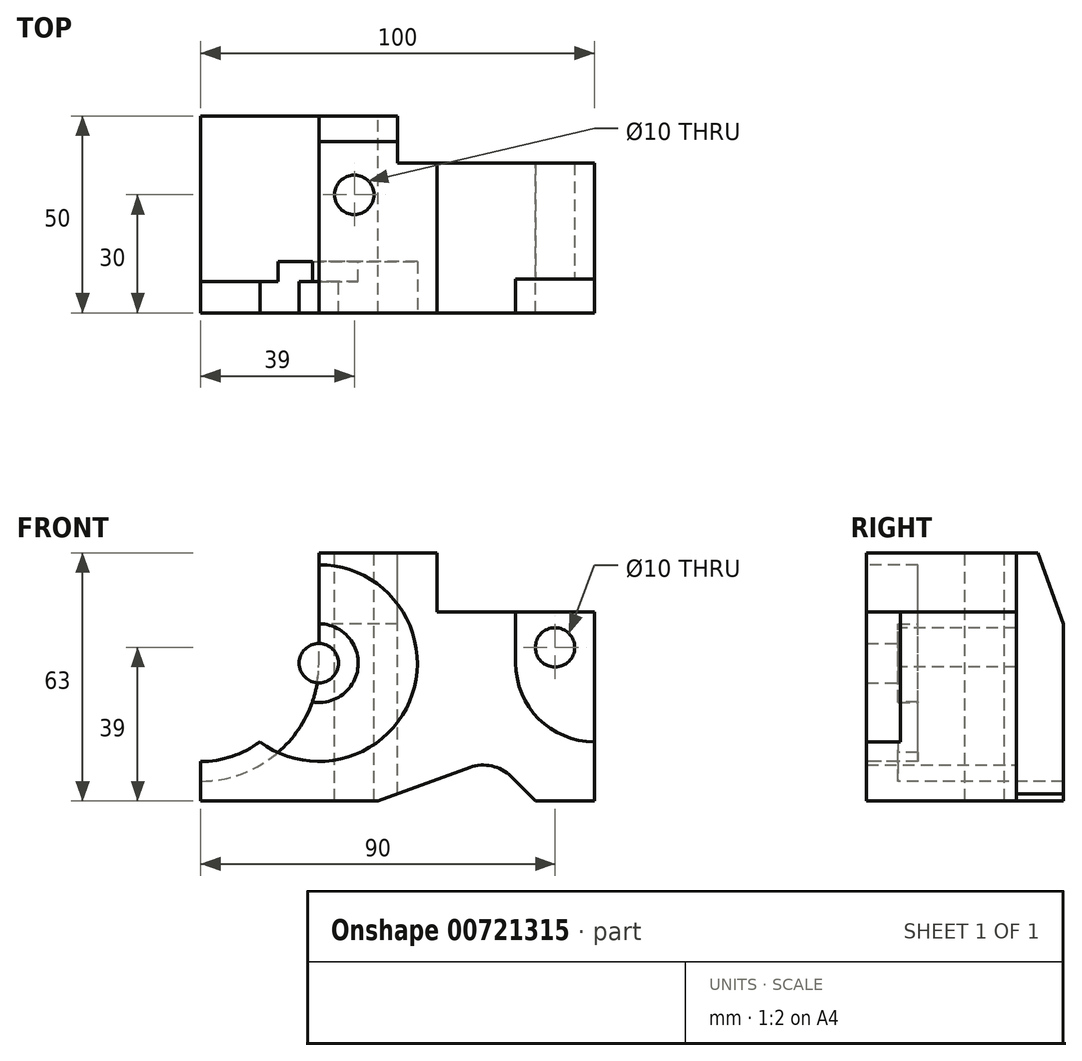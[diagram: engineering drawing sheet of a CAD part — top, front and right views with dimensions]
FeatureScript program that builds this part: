
annotation { "Feature Type Name" : "Feature", "Feature Type Description" : "" }
export const myFeature = defineFeature(function(context is Context, id is Id, definition is map)
    precondition{}
    {
        {
            var Q0;
            Q0=qCreatedBy(makeId("Front.planeOp"),FACE);
            var sketch = newSketch(context, id + "F0", { "sketchPlane" : qUnion([Q0])});
            skLineSegment(sketch, "E0.bottom", {"start": v(50, -31.5) * mm, "end": v(35, -31.5) * mm});
            skLineSegment(sketch, "E0.top", {"start": v(50, 31.5) * mm, "end": v(-50, 31.5) * mm});
            skLineSegment(sketch, "E0.left", {"start": v(50, -31.5) * mm, "end": v(50, 31.5) * mm});
            skLineSegment(sketch, "E0.right", {"start": v(-50, -31.5) * mm, "end": v(-50, 31.5) * mm});
            skPoint(sketch, "E0.middle", {"position": v(0, 0) * mm});
            skLineSegment(sketch, "E1", {"start": v(35, -31.5) * mm, "end": v(28.83, -25.33) * mm});
            skLineSegment(sketch, "E2", {"start": v(18.34, -23) * mm, "end": v(-5, -31.5) * mm});
            skLineSegment(sketch, "E3.trimOffspring", {"start": v(-5, -31.5) * mm, "end": v(-50, -31.5) * mm});
            skPoint(sketch, "E4.visualSharp", {"position": v(24.33, -20.83) * mm});
            skArc(sketch, "E4.filletArc", {"start": v(28.83, -25.33) * mm, "mid": v(23.92, -22.64) * mm, "end": v(18.34, -23) * mm});
            skSolve(sketch);
        }
        {
            var Q0;
            Q0 = qSketchRegion(id + "F0", true);
            extrude(context, id + "F1", {"entities" : qUnion([Q0]), "depth" : 50 * mm, "offsetDistance" : 25 * mm});
        }
        {
            var Q0;
            Q0=makeQuery(id+"F1.opExtrude","CAP_FACE",FACE,{"disambiguationData":[OSD([sQuery(id+"F0.wireOp",EDGE,"E0.bottom"),sQuery(id+"F0.wireOp",EDGE,"E0.top"),sQuery(id+"F0.wireOp",EDGE,"E0.left"),sQuery(id+"F0.wireOp",EDGE,"E0.right"),sQuery(id+"F0.wireOp",EDGE,"E1"),sQuery(id+"F0.wireOp",EDGE,"E2"),sQuery(id+"F0.wireOp",EDGE,"E3.trimOffspring"),sQuery(id+"F0.wireOp",EDGE,"E4.filletArc")])],"isStart":false});
            var sketch = newSketch(context, id + "F2", { "sketchPlane" : qUnion([Q0])});
            skPoint(sketch, "E5", {"position": v(50, 3.5) * mm});
            skArc(sketch, "E6", {"start": v(30, 3.5) * mm, "mid": v(35.86, -10.64) * mm, "end": v(50, -16.5) * mm});
            skLineSegment(sketch, "E7", {"start": v(30, 3.5) * mm, "end": v(30, 31.5) * mm});
            skLineSegment(sketch, "E8", {"start": v(30, 31.5) * mm, "end": v(50, 31.5) * mm});
            skLineSegment(sketch, "E9", {"start": v(50, 31.5) * mm, "end": v(50, -16.5) * mm});
            skSolve(sketch);
        }
        {
            var Q0;
            Q0 = qSketchRegion(id + "F2", true);
            extrude(context, id + "F3", {"entities" : qUnion([Q0]), "operationType" : NewBodyOperationType.REMOVE, "oppositeDirection" : true, "depth" : 8.57 * mm, "offsetDistance" : 25 * mm});
        }
        {
            var Q0;
            Q0=makeQuery(id+"F3.boolean.opBoolean","COPY",FACE,{"derivedFrom":makeQuery(id+"F3.opExtrude","CAP_FACE",FACE,{"disambiguationData":[OSD([sQuery(id+"F2.wireOp",EDGE,"E6"),sQuery(id+"F2.wireOp",EDGE,"E7"),sQuery(id+"F2.wireOp",EDGE,"E8"),sQuery(id+"F2.wireOp",EDGE,"E9")])],"isStart":false})});
            var sketch = newSketch(context, id + "F4", { "sketchPlane" : qUnion([Q0])});
            skCircle(sketch, "E10", {"center": v(40, 7.5) * mm, "radius": 5 * mm});
            skPoint(sketch, "E10.centerSnap0", {"position": v(50, 7.5) * mm});
            skSolve(sketch);
        }
        {
            var Q0;
            Q0 = qSketchRegion(id + "F4", true);
            extrude(context, id + "F5", {"entities" : qUnion([Q0]), "operationType" : NewBodyOperationType.REMOVE, "endBound" : BoundingType.THROUGH_ALL, "oppositeDirection" : true, "depth" : 25 * mm, "offsetDistance" : 25 * mm});
        }
        {
            var Q0;
            Q0=qCreatedBy(makeId("Front.planeOp"),FACE);
            var sketch = newSketch(context, id + "F6", { "sketchPlane" : qUnion([Q0])});
            skLineSegment(sketch, "E11.bottom", {"start": v(10, 31.5) * mm, "end": v(50, 31.5) * mm});
            skLineSegment(sketch, "E11.top", {"start": v(10, 16.5) * mm, "end": v(50, 16.5) * mm});
            skLineSegment(sketch, "E11.left", {"start": v(10, 31.5) * mm, "end": v(10, 16.5) * mm});
            skLineSegment(sketch, "E11.right", {"start": v(50, 31.5) * mm, "end": v(50, 16.5) * mm});
            skSolve(sketch);
        }
        {
            var Q0;
            Q0 = qSketchRegion(id + "F6", true);
            extrude(context, id + "F7", {"entities" : qUnion([Q0]), "operationType" : NewBodyOperationType.REMOVE, "endBound" : BoundingType.THROUGH_ALL, "depth" : 25 * mm, "offsetDistance" : 25 * mm});
        }
        {
            var Q0;
            Q0=makeQuery(id+"F1.opExtrude","SWEPT_FACE",FACE,{"disambiguationData":[OSD([sQuery(id+"F0.wireOp",EDGE,"E0.top")])]});
            var sketch = newSketch(context, id + "F8", { "sketchPlane" : qUnion([Q0])});
            skLineSegment(sketch, "E12.bottom", {"start": v(0, 0) * mm, "end": v(50, 0) * mm});
            skLineSegment(sketch, "E12.top", {"start": v(0, -12) * mm, "end": v(50, -12) * mm});
            skLineSegment(sketch, "E12.left", {"start": v(0, 0) * mm, "end": v(0, -12) * mm});
            skLineSegment(sketch, "E12.right", {"start": v(50, 0) * mm, "end": v(50, -12) * mm});
            skSolve(sketch);
        }
        {
            var Q0;
            Q0 = qSketchRegion(id + "F8", true);
            extrude(context, id + "F9", {"entities" : qUnion([Q0]), "operationType" : NewBodyOperationType.REMOVE, "endBound" : BoundingType.THROUGH_ALL, "oppositeDirection" : true, "depth" : 25 * mm, "offsetDistance" : 25 * mm});
        }
        {
            var Q0;
            Q0=makeQuery(id+"F1.opExtrude","CAP_FACE",FACE,{"disambiguationData":[OSD([sQuery(id+"F0.wireOp",EDGE,"E0.bottom"),sQuery(id+"F0.wireOp",EDGE,"E0.top"),sQuery(id+"F0.wireOp",EDGE,"E0.left"),sQuery(id+"F0.wireOp",EDGE,"E0.right"),sQuery(id+"F0.wireOp",EDGE,"E1"),sQuery(id+"F0.wireOp",EDGE,"E2"),sQuery(id+"F0.wireOp",EDGE,"E3.trimOffspring"),sQuery(id+"F0.wireOp",EDGE,"E4.filletArc")])],"isStart":false});
            cPlane(context, id + "F10", {"entities" : qUnion([Q0]), "cplaneType" : CPlaneType.OFFSET, "offset" : 8 * mm, "oppositeDirection" : true, "width" : 150 * mm, "height" : 150 * mm});
        }
        {
            var Q0;
            Q0=makeQuery(id+"F1.opExtrude","CAP_FACE",FACE,{"disambiguationData":[OSD([sQuery(id+"F0.wireOp",EDGE,"E0.bottom"),sQuery(id+"F0.wireOp",EDGE,"E0.top"),sQuery(id+"F0.wireOp",EDGE,"E0.left"),sQuery(id+"F0.wireOp",EDGE,"E0.right"),sQuery(id+"F0.wireOp",EDGE,"E1"),sQuery(id+"F0.wireOp",EDGE,"E2"),sQuery(id+"F0.wireOp",EDGE,"E3.trimOffspring"),sQuery(id+"F0.wireOp",EDGE,"E4.filletArc")])],"isStart":false});
            var sketch = newSketch(context, id + "F11", { "sketchPlane" : qUnion([Q0])});
            skCircle(sketch, "E13", {"center": v(-20, 3.5) * mm, "radius": 25 * mm});
            skSolve(sketch);
        }
        {
            var Q0;
            Q0 = qSketchRegion(id + "F11", true);
            extrude(context, id + "F12", {"entities" : qUnion([Q0]), "operationType" : NewBodyOperationType.REMOVE, "oppositeDirection" : true, "depth" : 13 * mm, "offsetDistance" : 25 * mm});
        }
        {
            var Q0;
            Q0=makeQuery(id+"F12.boolean.opBoolean","COPY",FACE,{"derivedFrom":makeQuery(id+"F12.opExtrude","CAP_FACE",FACE,{"disambiguationData":[OSD([sQuery(id+"F11.wireOp",EDGE,"E13")])],"isStart":false})});
            var sketch = newSketch(context, id + "F13", { "sketchPlane" : qUnion([Q0])});
            skCircle(sketch, "E14", {"center": v(-20, 3.5) * mm, "radius": 10 * mm});
            skSolve(sketch);
        }
        {
            var Q0;
            Q0 = qSketchRegion(id + "F13", true);
            extrude(context, id + "F14", {"entities" : qUnion([Q0]), "operationType" : NewBodyOperationType.ADD, "depth" : 5 * mm, "offsetDistance" : 25 * mm});
        }
        {
            var Q0;
            Q0=makeQuery(id+"F1.opExtrude","CAP_FACE",FACE,{"disambiguationData":[OSD([sQuery(id+"F0.wireOp",EDGE,"E0.bottom"),sQuery(id+"F0.wireOp",EDGE,"E0.top"),sQuery(id+"F0.wireOp",EDGE,"E0.left"),sQuery(id+"F0.wireOp",EDGE,"E0.right"),sQuery(id+"F0.wireOp",EDGE,"E1"),sQuery(id+"F0.wireOp",EDGE,"E2"),sQuery(id+"F0.wireOp",EDGE,"E3.trimOffspring"),sQuery(id+"F0.wireOp",EDGE,"E4.filletArc")])],"isStart":false});
            var sketch = newSketch(context, id + "F15", { "sketchPlane" : qUnion([Q0])});
            skArc(sketch, "E15", {"start": v(-50, -21.5) * mm, "mid": v(-32.32, -14.18) * mm, "end": v(-25, 3.5) * mm});
            skLineSegment(sketch, "E16", {"start": v(-25, 3.5) * mm, "end": v(-25, 31.5) * mm});
            skLineSegment(sketch, "E17", {"start": v(-25, 31.5) * mm, "end": v(-50, 31.5) * mm});
            skLineSegment(sketch, "E18", {"start": v(-50, 31.5) * mm, "end": v(-50, -21.5) * mm});
            skSolve(sketch);
        }
        {
            var Q0;
            Q0 = qSketchRegion(id + "F15", true);
            extrude(context, id + "F16", {"entities" : qUnion([Q0]), "operationType" : NewBodyOperationType.REMOVE, "endBound" : BoundingType.THROUGH_ALL, "oppositeDirection" : true, "depth" : 25 * mm, "offsetDistance" : 25 * mm});
        }
        {
            var Q0;
            Q0=qCreatedBy(id+"F10.planeOp",FACE);
            var sketch = newSketch(context, id + "F17", { "sketchPlane" : qUnion([Q0])});
            skArc(sketch, "E19", {"start": v(-50, -26.5) * mm, "mid": v(-28.79, -17.71) * mm, "end": v(-20, 3.5) * mm});
            skLineSegment(sketch, "E20", {"start": v(-20, 3.5) * mm, "end": v(-20, 31.5) * mm});
            skLineSegment(sketch, "E21", {"start": v(-20, 31.5) * mm, "end": v(-50, 31.5) * mm});
            skLineSegment(sketch, "E22", {"start": v(-50, 31.5) * mm, "end": v(-50, -26.5) * mm});
            skSolve(sketch);
        }
        {
            var Q0;
            Q0 = qSketchRegion(id + "F17", true);
            extrude(context, id + "F18", {"entities" : qUnion([Q0]), "operationType" : NewBodyOperationType.REMOVE, "endBound" : BoundingType.THROUGH_ALL, "oppositeDirection" : true, "depth" : 25 * mm, "offsetDistance" : 25 * mm});
        }
        {
            var Q0;
            Q0=makeQuery(id+"F1.opExtrude","CAP_FACE",FACE,{"disambiguationData":[OSD([sQuery(id+"F0.wireOp",EDGE,"E0.bottom"),sQuery(id+"F0.wireOp",EDGE,"E0.top"),sQuery(id+"F0.wireOp",EDGE,"E0.left"),sQuery(id+"F0.wireOp",EDGE,"E0.right"),sQuery(id+"F0.wireOp",EDGE,"E1"),sQuery(id+"F0.wireOp",EDGE,"E2"),sQuery(id+"F0.wireOp",EDGE,"E3.trimOffspring"),sQuery(id+"F0.wireOp",EDGE,"E4.filletArc")])],"isStart":false});
            var sketch = newSketch(context, id + "F19", { "sketchPlane" : qUnion([Q0])});
            skLineSegment(sketch, "E23.bottom", {"start": v(-25, 31.5) * mm, "end": v(-20, 31.5) * mm});
            skLineSegment(sketch, "E23.top", {"start": v(-25, 25.55) * mm, "end": v(-20, 25.55) * mm});
            skLineSegment(sketch, "E23.left", {"start": v(-25, 31.5) * mm, "end": v(-25, 25.55) * mm});
            skLineSegment(sketch, "E23.right", {"start": v(-20, 31.5) * mm, "end": v(-20, 25.55) * mm});
            skSolve(sketch);
        }
        {
            var Q0;
            Q0 = qSketchRegion(id + "F19", true);
            extrude(context, id + "F20", {"entities" : qUnion([Q0]), "operationType" : NewBodyOperationType.REMOVE, "oppositeDirection" : true, "depth" : 25 * mm, "offsetDistance" : 25 * mm});
        }
        {
            var Q0;
            Q0=makeQuery(id+"F14.opExtrude","CAP_FACE",FACE,{"disambiguationData":[OSD([sQuery(id+"F13.wireOp",EDGE,"E14")])],"isStart":false});
            var sketch = newSketch(context, id + "F21", { "sketchPlane" : qUnion([Q0])});
            skCircle(sketch, "E24", {"center": v(-20, 3.5) * mm, "radius": 5 * mm});
            skSolve(sketch);
        }
        {
            var Q0;
            Q0 = qSketchRegion(id + "F21", true);
            extrude(context, id + "F22", {"entities" : qUnion([Q0]), "operationType" : NewBodyOperationType.ADD, "depth" : 8 * mm, "offsetDistance" : 25 * mm});
        }
        {
            var Q0;
            Q0=makeQuery(id+"F1.opExtrude","SWEPT_FACE",FACE,{"disambiguationData":[OSD([sQuery(id+"F0.wireOp",EDGE,"E0.top")])]});
            var sketch = newSketch(context, id + "F23", { "sketchPlane" : qUnion([Q0])});
            skCircle(sketch, "E25", {"center": v(-11, -20) * mm, "radius": 5 * mm});
            skSolve(sketch);
        }
        {
            var Q0;
            Q0 = qSketchRegion(id + "F23", true);
            extrude(context, id + "F24", {"entities" : qUnion([Q0]), "operationType" : NewBodyOperationType.REMOVE, "endBound" : BoundingType.THROUGH_ALL, "oppositeDirection" : true, "depth" : 25 * mm, "offsetDistance" : 25 * mm});
        }
        {
            var Q0;
            Q0=makeQuery(id+"F20.boolean.opBoolean","MERGE",FACE,{"derivedFrom":[makeQuery(id+"F18.boolean.opBoolean","COPY",FACE,{"derivedFrom":makeQuery(id+"F18.opExtrude","SWEPT_FACE",FACE,{"disambiguationData":[OSD([sQuery(id+"F17.wireOp",EDGE,"E20")])]})}),makeQuery(id+"F20.opExtrude","SWEPT_FACE",FACE,{"disambiguationData":[OSD([sQuery(id+"F19.wireOp",EDGE,"E23.right")])]})]});
            var sketch = newSketch(context, id + "F25", { "sketchPlane" : qUnion([Q0])});
            skLineSegment(sketch, "E26", {"start": v(0, 13.5) * mm, "end": v(6.55, 31.5) * mm});
            skLineSegment(sketch, "E27", {"start": v(6.55, 31.5) * mm, "end": v(0, 31.5) * mm});
            skLineSegment(sketch, "E28", {"start": v(0, 31.5) * mm, "end": v(0, 13.5) * mm});
            skSolve(sketch);
        }
        {
            var Q0;
            Q0 = qSketchRegion(id + "F25", true);
            extrude(context, id + "F26", {"entities" : qUnion([Q0]), "operationType" : NewBodyOperationType.REMOVE, "endBound" : BoundingType.THROUGH_ALL, "oppositeDirection" : true, "depth" : 25 * mm, "offsetDistance" : 25 * mm});
        }
    });
